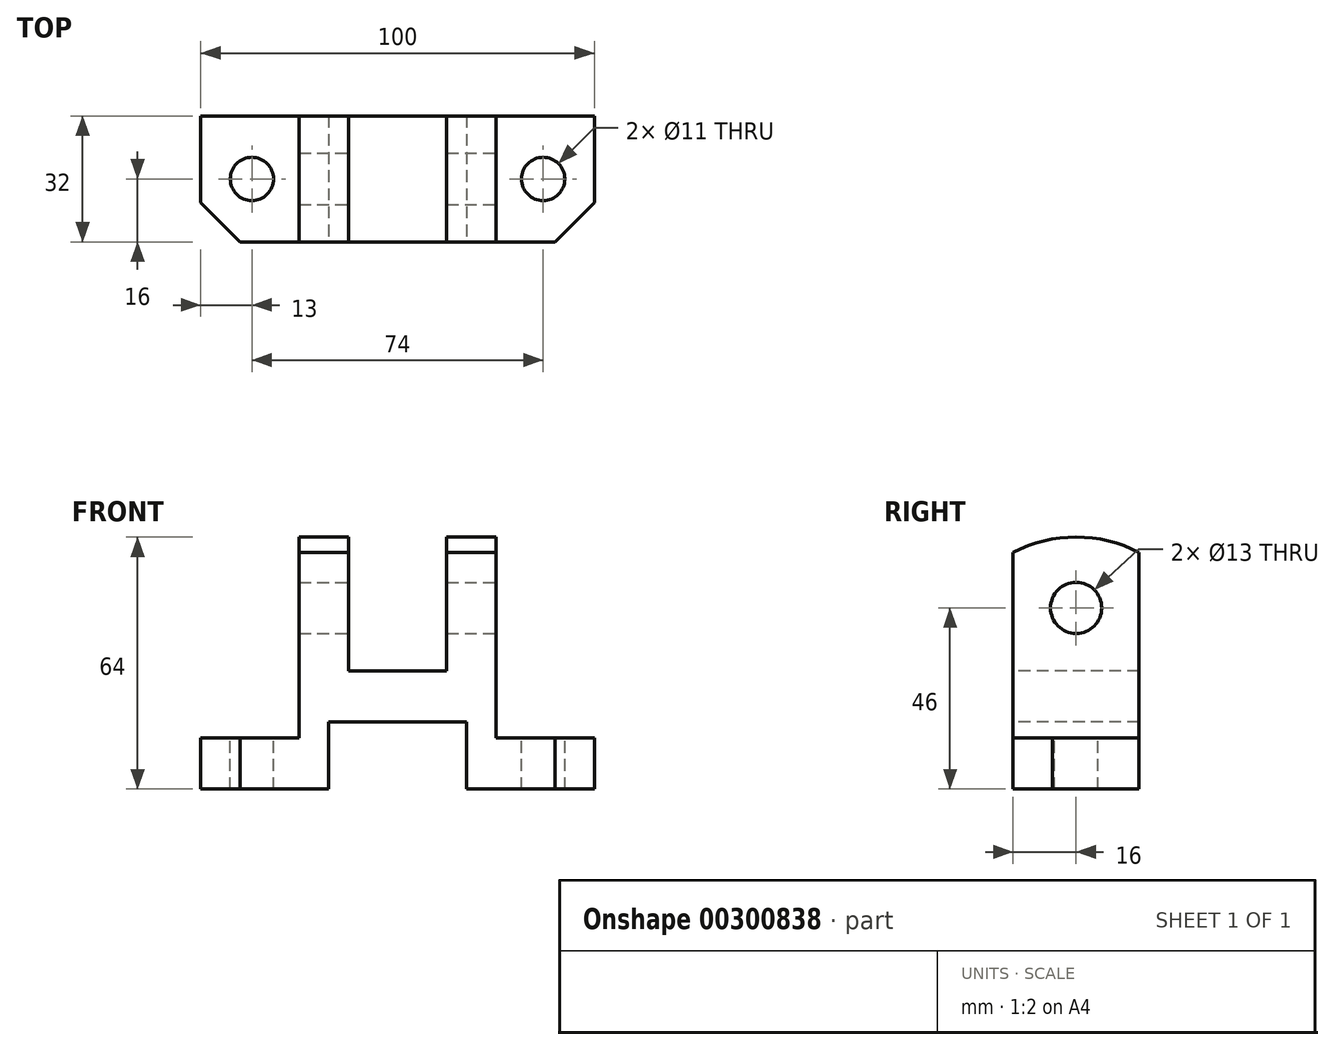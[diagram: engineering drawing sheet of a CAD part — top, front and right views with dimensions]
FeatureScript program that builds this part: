
annotation { "Feature Type Name" : "Feature", "Feature Type Description" : "" }
export const myFeature = defineFeature(function(context is Context, id is Id, definition is map)
    precondition{}
    {
        {
            var Q0;
            Q0=qCreatedBy(makeId("Right.planeOp"),FACE);
            var sketch = newSketch(context, id + "F0", { "sketchPlane" : qUnion([Q0])});
            skLineSegment(sketch, "E0", {"start": v(-16, 0) * mm, "end": v(16, 0) * mm});
            skLineSegment(sketch, "E1", {"start": v(16, 0) * mm, "end": v(16, 60.13) * mm});
            skLineSegment(sketch, "E2", {"start": v(-16, 0) * mm, "end": v(-16, 60.13) * mm});
            skArc(sketch, "E3", {"start": v(16, 60.13) * mm, "mid": v(0, 64) * mm, "end": v(-16, 60.13) * mm});
            skSolve(sketch);
        }
        {
            var Q0;
            Q0 = qSketchRegion(id + "F0", true);
            extrude(context, id + "F1", {"entities" : qUnion([Q0]), "endBound" : BoundingType.SYMMETRIC, "depth" : 100 * mm});
        }
        {
            var Q0;
            Q0=makeQuery(id+"F1.opExtrude","SWEPT_FACE",FACE,{"disambiguationData":[OSD([sQuery(id+"F0.wireOp",EDGE,"E2")])]});
            var sketch = newSketch(context, id + "F2", { "sketchPlane" : qUnion([Q0])});
            skLineSegment(sketch, "E4.bottom", {"start": v(-17.5, 0) * mm, "end": v(17.5, 0) * mm});
            skLineSegment(sketch, "E4.top", {"start": v(-17.5, 17) * mm, "end": v(17.5, 17) * mm});
            skLineSegment(sketch, "E4.left", {"start": v(-17.5, 0) * mm, "end": v(-17.5, 17) * mm});
            skLineSegment(sketch, "E4.right", {"start": v(17.5, 0) * mm, "end": v(17.5, 17) * mm});
            skLineSegment(sketch, "E5.bottom", {"start": v(-12.5, 30) * mm, "end": v(12.5, 30) * mm});
            skLineSegment(sketch, "E5.top", {"start": v(-12.5, 70.24) * mm, "end": v(12.5, 70.24) * mm});
            skLineSegment(sketch, "E5.left", {"start": v(-12.5, 30) * mm, "end": v(-12.5, 70.24) * mm});
            skLineSegment(sketch, "E5.right", {"start": v(12.5, 30) * mm, "end": v(12.5, 70.24) * mm});
            skLineSegment(sketch, "E6.bottom", {"start": v(-50, 13) * mm, "end": v(-25, 13) * mm});
            skLineSegment(sketch, "E6.top", {"start": v(-50, 73.4) * mm, "end": v(-25, 73.4) * mm});
            skLineSegment(sketch, "E6.left", {"start": v(-50, 13) * mm, "end": v(-50, 73.4) * mm});
            skLineSegment(sketch, "E6.right", {"start": v(-25, 13) * mm, "end": v(-25, 73.4) * mm});
            skLineSegment(sketch, "E7.bottom", {"start": v(50, 13) * mm, "end": v(25, 13) * mm});
            skLineSegment(sketch, "E7.top", {"start": v(50, 73.4) * mm, "end": v(25, 73.4) * mm});
            skLineSegment(sketch, "E7.left", {"start": v(50, 13) * mm, "end": v(50, 73.4) * mm});
            skLineSegment(sketch, "E7.right", {"start": v(25, 13) * mm, "end": v(25, 73.4) * mm});
            skSolve(sketch);
        }
        {
            var Q0;
            Q0 = qSketchRegion(id + "F2", true);
            extrude(context, id + "F3", {"entities" : qUnion([Q0]), "operationType" : NewBodyOperationType.REMOVE, "endBound" : BoundingType.THROUGH_ALL, "oppositeDirection" : true, "depth" : 25 * mm});
        }
        {
            var Q0;
            Q0=makeQuery(id+"F3.boolean.opBoolean","COPY",FACE,{"derivedFrom":makeQuery(id+"F3.opExtrude","SWEPT_FACE",FACE,{"disambiguationData":[OSD([sQuery(id+"F2.wireOp",EDGE,"E6.bottom")])]})});
            var sketch = newSketch(context, id + "F4", { "sketchPlane" : qUnion([Q0])});
            skLineSegment(sketch, "E8", {"start": v(-50, -6) * mm, "end": v(-40, -16) * mm});
            skLineSegment(sketch, "E9", {"start": v(-40, -16) * mm, "end": v(-50, -16) * mm});
            skLineSegment(sketch, "E10", {"start": v(-50, -16) * mm, "end": v(-50, -6) * mm});
            skCircle(sketch, "E11", {"center": v(-37, 0) * mm, "radius": 5.5 * mm});
            skPoint(sketch, "E11.centerSnap0", {"position": v(-50, 0) * mm});
            skSolve(sketch);
        }
        {
            var Q0;
            Q0 = qSketchRegion(id + "F4", true);
            extrude(context, id + "F5", {"entities" : qUnion([Q0]), "operationType" : NewBodyOperationType.REMOVE, "endBound" : BoundingType.THROUGH_ALL, "oppositeDirection" : true, "depth" : 25 * mm});
        }
        {
            var Q0;
            Q0=makeQuery(id+"F3.boolean.opBoolean","COPY",FACE,{"derivedFrom":makeQuery(id+"F3.opExtrude","SWEPT_FACE",FACE,{"disambiguationData":[OSD([sQuery(id+"F2.wireOp",EDGE,"E7.bottom")])]})});
            var sketch = newSketch(context, id + "F6", { "sketchPlane" : qUnion([Q0])});
            skLineSegment(sketch, "E12", {"start": v(40, -16) * mm, "end": v(50, -16) * mm});
            skLineSegment(sketch, "E13", {"start": v(50, -16) * mm, "end": v(50, -6) * mm});
            skLineSegment(sketch, "E14", {"start": v(50, -6) * mm, "end": v(40, -16) * mm});
            skCircle(sketch, "E15", {"center": v(37, 0) * mm, "radius": 5.5 * mm});
            skSolve(sketch);
        }
        {
            var Q0;
            Q0 = qSketchRegion(id + "F6", true);
            extrude(context, id + "F7", {"entities" : qUnion([Q0]), "operationType" : NewBodyOperationType.REMOVE, "endBound" : BoundingType.THROUGH_ALL, "oppositeDirection" : true, "depth" : 25 * mm});
        }
        {
            var Q0;
            Q0=makeQuery(id+"F3.boolean.opBoolean","COPY",FACE,{"derivedFrom":makeQuery(id+"F3.opExtrude","SWEPT_FACE",FACE,{"disambiguationData":[OSD([sQuery(id+"F2.wireOp",EDGE,"E7.right")])]})});
            var sketch = newSketch(context, id + "F8", { "sketchPlane" : qUnion([Q0])});
            skCircle(sketch, "E16", {"center": v(0, 46) * mm, "radius": 6.5 * mm});
            skSolve(sketch);
        }
        {
            var Q0;
            Q0 = qSketchRegion(id + "F8", true);
            extrude(context, id + "F9", {"entities" : qUnion([Q0]), "operationType" : NewBodyOperationType.REMOVE, "endBound" : BoundingType.THROUGH_ALL, "oppositeDirection" : true, "depth" : 25 * mm});
        }
    });
